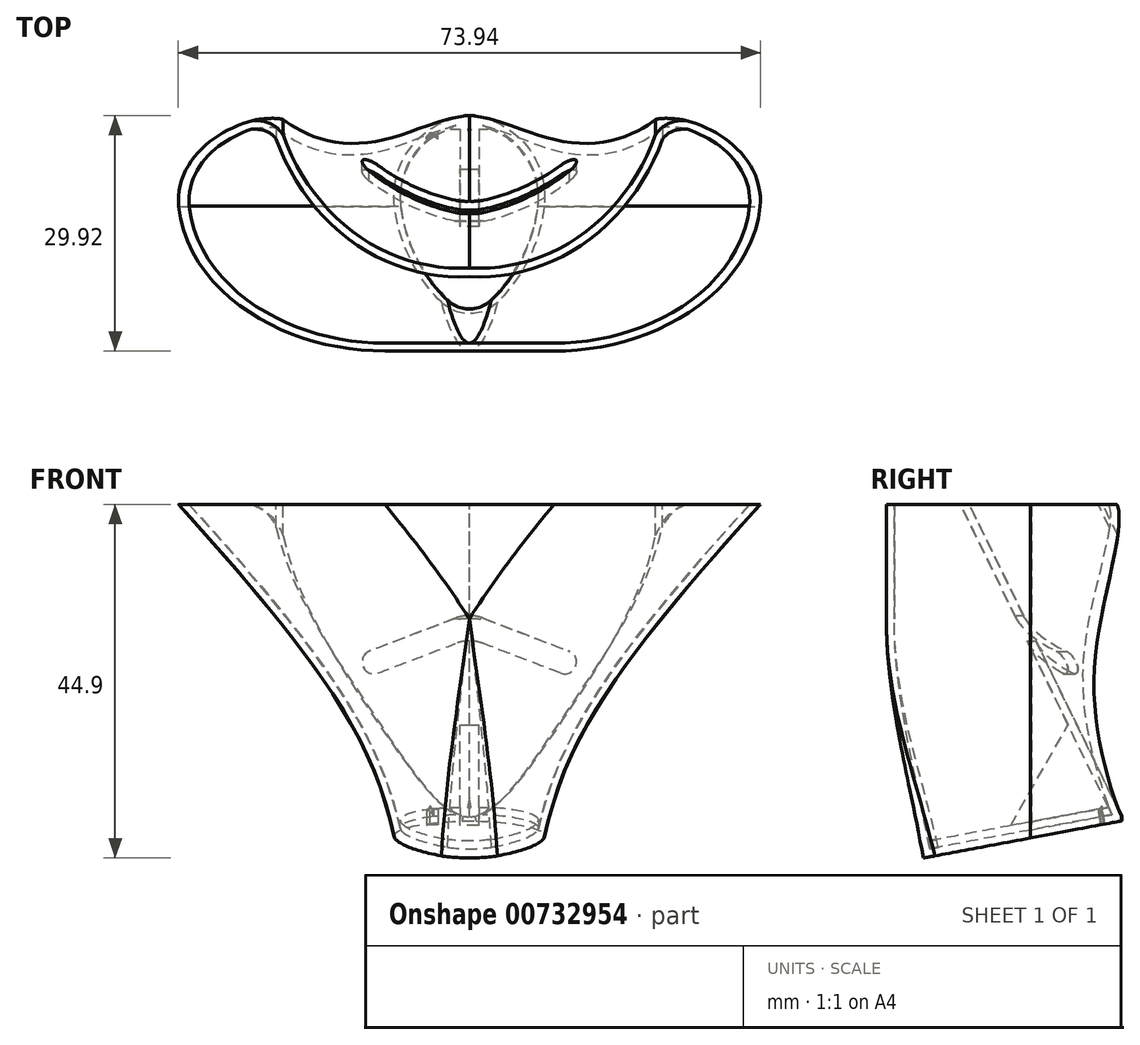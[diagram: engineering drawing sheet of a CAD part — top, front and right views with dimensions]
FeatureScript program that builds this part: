
annotation { "Feature Type Name" : "Feature", "Feature Type Description" : "" }
export const myFeature = defineFeature(function(context is Context, id is Id, definition is map)
    precondition{}
    {
        {
            var Q0;
            Q0=qCreatedBy(makeId("Front.planeOp"),FACE);
            var sketch = newSketch(context, id + "F0", { "sketchPlane" : qUnion([Q0])});
            skLineSegment(sketch, "E0", {"start": v(-9, -21.86) * mm, "end": v(9, -21.86) * mm});
            skLineSegment(sketch, "E1", {"start": v(0, -21.86) * mm, "end": v(0, 23.14) * mm, "construction": true});
            skLineSegment(sketch, "E2", {"start": v(-37, 23.14) * mm, "end": v(37, 23.14) * mm});
            skFitSpline(sketch, "E3", {"points": [v(-37, 23.14) * mm, v(-9, -21.86) * mm], "startDerivative": vector(66.87, -73.39) * mm, "endDerivative": vector(7.33, -37.29) * mm});
            skFitSpline(sketch, "E4.MirrorCS", {"points": [v(37, 23.14) * mm, v(9, -21.86) * mm], "startDerivative": vector(-66.87, -73.39) * mm, "endDerivative": vector(-7.33, -37.29) * mm});
            skSolve(sketch);
        }
        {
            var Q0;
            Q0=makeQuery(id+"F0.imprint","IMPRINT",FACE,{"disambiguationData":[TD([[makeQuery(id+"F0.imprint","IMPRINT",EDGE,{"derivedFrom":sQuery(id+"F0.wireOp",EDGE,"E0")}),1.0]])]});
            extrude(context, id + "F1", {"entities" : qUnion([Q0]), "depth" : 30 * mm, "offsetDistance" : 25 * mm});
        }
        {
            var Q0;
            Q0=makeQuery(id+"F1.opExtrude","CAP_EDGE",EDGE,{"disambiguationData":[OSD([sQuery(id+"F0.wireOp",EDGE,"E3")])],"isStart":false});
            var Q1;
            Q1=makeQuery(id+"F1.opExtrude","CAP_EDGE",EDGE,{"disambiguationData":[OSD([sQuery(id+"F0.wireOp",EDGE,"E4.MirrorCS")])],"isStart":false});
            fillet(context, id + "F2", {"entities" : qUnion([Q0, Q1]), "radius" : 19.8 * mm, "tangentPropagation" : true, "allowEdgeOverflow" : false});
        }
        {
            var Q0;
            Q0=makeQuery(id+"F1.opExtrude","CAP_EDGE",EDGE,{"disambiguationData":[OSD([sQuery(id+"F0.wireOp",EDGE,"E3")])],"isStart":true});
            var Q1;
            Q1=makeQuery(id+"F1.opExtrude","CAP_EDGE",EDGE,{"disambiguationData":[OSD([sQuery(id+"F0.wireOp",EDGE,"E4.MirrorCS")])],"isStart":true});
            fillet(context, id + "F3", {"entities" : qUnion([Q0, Q1]), "radius" : 10.86 * mm, "tangentPropagation" : true, "allowEdgeOverflow" : false});
        }
        {
            var Q0;
            Q0=makeQuery(id+"F2.opFillet","BLEND_EDGE",EDGE,{"blendedFrom":[makeQuery(id+"F1.opExtrude","CAP_EDGE",EDGE,{"disambiguationData":[OSD([sQuery(id+"F0.wireOp",EDGE,"E3")])],"isStart":false}),makeQuery(id+"F1.opExtrude","CAP_EDGE",EDGE,{"disambiguationData":[OSD([sQuery(id+"F0.wireOp",EDGE,"E4.MirrorCS")])],"isStart":false})],"blendedInto":[]});
            fillet(context, id + "F4", {"entities" : qUnion([Q0]), "radius" : 5 * mm, "tangentPropagation" : true, "allowEdgeOverflow" : false});
        }
        {
            var Q0;
            Q0=makeQuery(id+"F3.opFillet","BLEND_EDGE",EDGE,{"blendedFrom":[makeQuery(id+"F1.opExtrude","CAP_EDGE",EDGE,{"disambiguationData":[OSD([sQuery(id+"F0.wireOp",EDGE,"E3")])],"isStart":true}),makeQuery(id+"F1.opExtrude","CAP_EDGE",EDGE,{"disambiguationData":[OSD([sQuery(id+"F0.wireOp",EDGE,"E4.MirrorCS")])],"isStart":true})],"blendedInto":[]});
            fillet(context, id + "F5", {"entities" : qUnion([Q0]), "radius" : 5 * mm, "tangentPropagation" : true, "allowEdgeOverflow" : false});
        }
        {
            var Q0;
            Q0=qCreatedBy(makeId("Right.planeOp"),FACE);
            var sketch = newSketch(context, id + "F6", { "sketchPlane" : qUnion([Q0])});
            skLineSegment(sketch, "E5", {"start": v(-31.86, -23) * mm, "end": v(8.16, -15.5) * mm});
            skLineSegment(sketch, "E6", {"start": v(8.16, -15.5) * mm, "end": v(3.01, -25.08) * mm});
            skLineSegment(sketch, "E7", {"start": v(3.01, -25.08) * mm, "end": v(-31.86, -23) * mm});
            skSolve(sketch);
        }
        {
            var Q0;
            Q0=qSketchRegion(id+"F6",true);
            extrude(context, id + "F7", {"entities" : qUnion([Q0]), "operationType" : NewBodyOperationType.REMOVE, "depth" : 25 * mm, "offsetDistance" : 25 * mm, "hasSecondDirection" : true, "secondDirectionOppositeDirection" : true, "secondDirectionDepth" : 25 * mm});
        }
        {
            var Q0;
            Q0=qCreatedBy(makeId("Right.planeOp"),FACE);
            var sketch = newSketch(context, id + "F8", { "sketchPlane" : qUnion([Q0])});
            skLineSegment(sketch, "E8", {"start": v(-24.08, 32.66) * mm, "end": v(0, 44.42) * mm});
            skSolve(sketch);
        }
        {
            var Q0;
            Q0=sQuery(id+"F8.wireOp",EDGE,"E8");
            extrude(context, id + "F9", {"bodyType" : ToolBodyType.SURFACE, "surfaceEntities" : qUnion([Q0]), "depth" : 25 * mm, "offsetDistance" : 25 * mm, "hasSecondDirection" : true, "secondDirectionOppositeDirection" : true, "secondDirectionDepth" : 25 * mm});
        }
        {
            var Q0;
            Q0=makeQuery(id+"F9.opExtrude","SWEPT_FACE",FACE,{"disambiguationData":[OSD([sQuery(id+"F8.wireOp",EDGE,"E8")])]});
            var sketch = newSketch(context, id + "F10", { "sketchPlane" : qUnion([Q0])});
            skArc(sketch, "E9", {"start": v(23.67, -7.9) * mm, "mid": v(14.28, 3.52) * mm, "end": v(0, 7.3) * mm});
            skFitSpline(sketch, "E10", {"points": [v(23.67, -7.9) * mm, v(31.63, -8.58) * mm], "startDerivative": vector(3.77, -5) * mm, "endDerivative": vector(13, 4.88) * mm});
            skLineSegment(sketch, "E11", {"start": v(31.63, -8.58) * mm, "end": v(10.84, -28.18) * mm});
            skLineSegment(sketch, "E12", {"start": v(10.84, -28.18) * mm, "end": v(0, -18.9) * mm});
            skLineSegment(sketch, "E13", {"start": v(0, 4.27) * mm, "end": v(0, -45.58) * mm, "construction": true});
            skFitSpline(sketch, "E14.MirrorCS", {"points": [v(-23.67, -7.9) * mm, v(-31.63, -8.58) * mm], "startDerivative": vector(-3.77, -5) * mm, "endDerivative": vector(-13, 4.88) * mm});
            skLineSegment(sketch, "E15.MirrorCS", {"start": v(-31.63, -8.58) * mm, "end": v(-10.84, -28.18) * mm});
            skLineSegment(sketch, "E16.MirrorCS", {"start": v(-10.84, -28.18) * mm, "end": v(0, -18.9) * mm});
            skArc(sketch, "E17.MirrorCS", {"start": v(-23.67, -7.9) * mm, "mid": v(-14.28, 3.52) * mm, "end": v(0, 7.3) * mm});
            skPoint(sketch, "E18.orphan", {"position": v(-24.25, -9.56) * mm});
            skPoint(sketch, "E19.orphan", {"position": v(24.25, -9.56) * mm});
            skSolve(sketch);
        }
        {
            var Q0;
            Q0=qSketchRegion(id+"F10",true);
            extrude(context, id + "F11", {"entities" : qUnion([Q0]), "operationType" : NewBodyOperationType.REMOVE, "depth" : 77.2 * mm, "offsetDistance" : 25 * mm});
        }
        {
            var Q0;
            Q0=makeQuery(id+"F9.opExtrude","SWEPT_BODY",BODY,{"disambiguationData":[OSD([sQuery(id+"F8.wireOp",EDGE,"E8")])]});
            deleteBodies(context, id + "F12", {"entities" : qUnion([Q0])});
        }
        {
            var Q0;
            Q0=makeQuery(id+"F1.opExtrude","SWEPT_FACE",FACE,{"disambiguationData":[OSD([sQuery(id+"F0.wireOp",EDGE,"E2")])]});
            shell(context, id + "F13", {"entities" : qUnion([Q0]), "thickness" : 1 * mm});
        }
        {
            var Q0;
            Q0=makeQuery(id+"F7.boolean.opBoolean","COPY",FACE,{"derivedFrom":makeQuery(id+"F7.opExtrude","SWEPT_FACE",FACE,{"disambiguationData":[OSD([sQuery(id+"F6.wireOp",EDGE,"E5")])]})});
            var sketch = newSketch(context, id + "F14", { "sketchPlane" : qUnion([Q0])});
            skFitSpline(sketch, "E20", {"points": [v(-5.51, 5.37) * mm, v(-4, 5.85) * mm, v(-3.4, 8.02) * mm, v(-5.7, 12.02) * mm, v(-4.58, 21.11) * mm, v(0, 25.37) * mm], "startDerivative": vector(11.33, -0.98) * mm, "endDerivative": vector(15.89, -0.05) * mm});
            skFitSpline(sketch, "E21.MirrorCS", {"points": [v(5.51, 5.37) * mm, v(4, 5.85) * mm, v(3.4, 8.02) * mm, v(5.7, 12.02) * mm, v(4.58, 21.11) * mm, v(0, 25.37) * mm], "startDerivative": vector(-11.33, -0.98) * mm, "endDerivative": vector(-15.89, -0.05) * mm});
            skFitSpline(sketch, "E22", {"points": [v(0, 27.88) * mm, v(-2.51, 27.15) * mm, v(-6.1, 22.7) * mm, v(-7.89, 18.78) * mm, v(-8.68, 15.18) * mm, v(-8.46, 11.07) * mm, v(-6.69, 7.46) * mm, v(-4.98, 5.4) * mm], "startDerivative": vector(-23.61, -0.54) * mm, "endDerivative": vector(20.39, -26.15) * mm});
            skArc(sketch, "E23.filletArc", {"start": v(-5.43, 5.96) * mm, "mid": v(-4.73, 5.6) * mm, "end": v(-3.99, 5.85) * mm});
            skFitSpline(sketch, "E24.MirrorCS", {"points": [v(0, 27.88) * mm, v(2.51, 27.15) * mm, v(6.1, 22.7) * mm, v(7.89, 18.78) * mm, v(8.68, 15.18) * mm, v(8.46, 11.07) * mm, v(6.69, 7.46) * mm, v(4.98, 5.4) * mm], "startDerivative": vector(23.61, -0.54) * mm, "endDerivative": vector(-20.39, -26.15) * mm});
            skArc(sketch, "E25.MirrorCS", {"start": v(5.43, 5.96) * mm, "mid": v(4.73, 5.6) * mm, "end": v(3.99, 5.85) * mm});
            skSolve(sketch);
        }
        {
            var Q0;
            Q0=makeQuery(id+"F14.imprint","IMPRINT",FACE,{"disambiguationData":[TD([[makeQuery(id+"F14.imprint","IMPRINT",EDGE,{"derivedFrom":sQuery(id+"F14.wireOp",EDGE,"E20")}),1.0]])]});
            extrude(context, id + "F15", {"entities" : qUnion([Q0]), "operationType" : NewBodyOperationType.REMOVE, "oppositeDirection" : true, "depth" : 3 * mm, "offsetDistance" : 25 * mm});
        }
        {
            var Q0;
            Q0=qCreatedBy(makeId("Right.planeOp"),FACE);
            var sketch = newSketch(context, id + "F16", { "sketchPlane" : qUnion([Q0])});
            skLineSegment(sketch, "E26", {"start": v(-14.52, -18.2) * mm, "end": v(-6.85, -4.74) * mm});
            skLineSegment(sketch, "E27", {"start": v(-6.85, -4.74) * mm, "end": v(-1.66, -15.56) * mm});
            skLineSegment(sketch, "E28", {"start": v(-1.66, -15.56) * mm, "end": v(-14.52, -18.2) * mm});
            skSolve(sketch);
        }
        {
            var Q0;
            Q0=qSketchRegion(id+"F16",true);
            extrude(context, id + "F17", {"entities" : qUnion([Q0]), "operationType" : NewBodyOperationType.ADD, "depth" : 1.2 * mm, "offsetDistance" : 25 * mm, "hasSecondDirection" : true, "secondDirectionOppositeDirection" : true, "secondDirectionDepth" : 1.2 * mm});
        }
        {
            var Q0;
            Q0=makeQuery(id+"F14.imprint","IMPRINT",FACE,{"disambiguationData":[TD([[makeQuery(id+"F14.imprint","IMPRINT",EDGE,{"derivedFrom":sQuery(id+"F14.wireOp",EDGE,"E20")}),1.0]])]});
            extrude(context, id + "F18", {"entities" : qUnion([Q0]), "operationType" : NewBodyOperationType.REMOVE, "oppositeDirection" : true, "depth" : 3 * mm, "offsetDistance" : 25 * mm});
        }
        {
            var Q0;
            Q0=qCreatedBy(makeId("Front.planeOp"),FACE);
            var sketch = newSketch(context, id + "F19", { "sketchPlane" : qUnion([Q0])});
            skPoint(sketch, "E29.middle", {"position": v(0, 3.9) * mm});
            skLineSegment(sketch, "E30", {"start": v(11.58, 1.73) * mm, "end": v(1.79, 5.48) * mm});
            skLineSegment(sketch, "E31", {"start": v(1.79, 8.7) * mm, "end": v(12.73, 4.5) * mm});
            skLineSegment(sketch, "E32.MirrorCS", {"start": v(-1.79, 8.7) * mm, "end": v(-12.73, 4.5) * mm});
            skLineSegment(sketch, "E33.MirrorCS", {"start": v(-11.58, 1.73) * mm, "end": v(-1.79, 5.48) * mm});
            skArc(sketch, "E34", {"start": v(11.58, 1.73) * mm, "mid": v(13.5, 2.56) * mm, "end": v(12.73, 4.5) * mm});
            skArc(sketch, "E35.MirrorCS", {"start": v(-11.58, 1.73) * mm, "mid": v(-13.5, 2.56) * mm, "end": v(-12.73, 4.5) * mm});
            skPoint(sketch, "E36.visualSharp", {"position": v(0, 9.38) * mm});
            skArc(sketch, "E36.filletArc", {"start": v(1.79, 8.7) * mm, "mid": v(0, 9.02) * mm, "end": v(-1.79, 8.7) * mm});
            skPoint(sketch, "E37.visualSharp", {"position": v(0, 6.16) * mm});
            skArc(sketch, "E37.filletArc", {"start": v(1.79, 5.48) * mm, "mid": v(0, 5.8) * mm, "end": v(-1.79, 5.48) * mm});
            skSolve(sketch);
        }
        {
            var Q0;
            Q0=qSketchRegion(id+"F19",true);
            extrude(context, id + "F20", {"entities" : qUnion([Q0]), "operationType" : NewBodyOperationType.REMOVE, "depth" : 13.5 * mm, "offsetDistance" : 25 * mm});
        }
        {
            var Q0;
            Q0=makeQuery(id+"F15.boolean.opBoolean","SPLIT",FACE,{"disambiguationData":[TD([makeQuery(id+"F13.opShell","OFFSET_FACE",FACE,{"disambiguationData":[OSD([sQuery(id+"F10.wireOp",EDGE,"E9")])]})])],"derivedFrom":makeQuery(id+"F13.opShell","OFFSET_FACE",FACE,{"disambiguationData":[OSD([sQuery(id+"F6.wireOp",EDGE,"E5")])]})});
            extrude(context, id + "F21", {"entities" : qUnion([Q0]), "operationType" : NewBodyOperationType.ADD, "depth" : 1 * mm, "offsetDistance" : 25 * mm});
        }
    });
